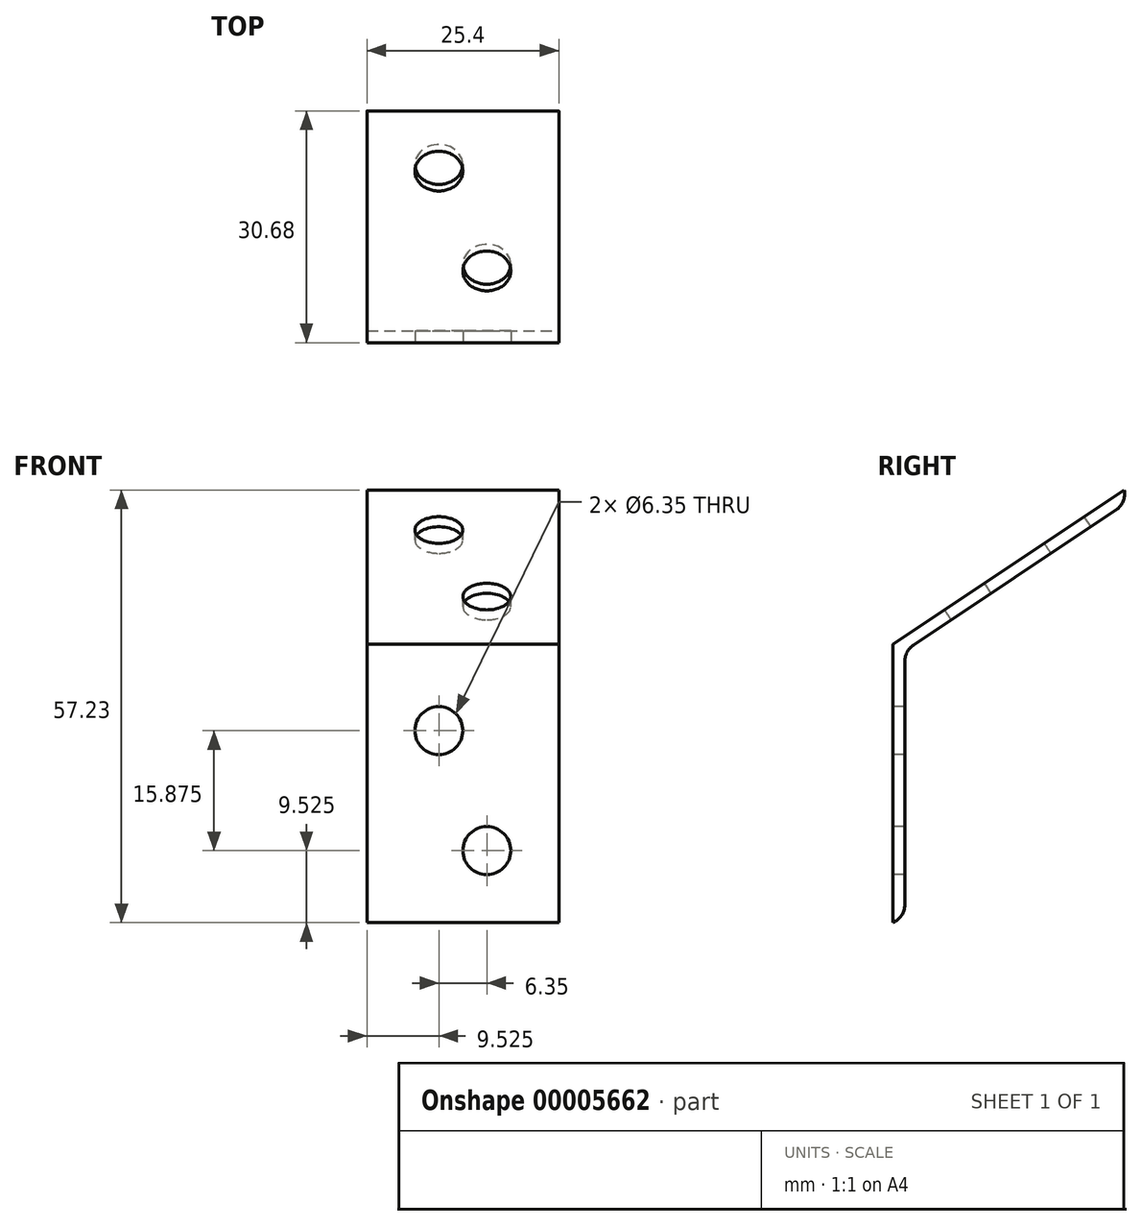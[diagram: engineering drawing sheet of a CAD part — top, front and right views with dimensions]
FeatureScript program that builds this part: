
annotation { "Feature Type Name" : "Feature", "Feature Type Description" : "" }
export const myFeature = defineFeature(function(context is Context, id is Id, definition is map)
    precondition{}
    {
        {
            var Q0;
            Q0=qCreatedBy(makeId("Right.planeOp"),FACE);
            var sketch = newSketch(context, id + "F0", { "sketchPlane" : qUnion([Q0])});
            skLineSegment(sketch, "E0.bottom", {"start": v(0, 0) * mm, "end": v(-1.59, 0) * mm});
            skLineSegment(sketch, "E0.left", {"start": v(0, 0) * mm, "end": v(0, 38.1) * mm});
            skLineSegment(sketch, "E0.right", {"start": v(-1.59, 0) * mm, "end": v(-1.59, 38.95) * mm});
            skLineSegment(sketch, "E1", {"start": v(0, 38.1) * mm, "end": v(31.7, 59.23) * mm});
            skLineSegment(sketch, "E2", {"start": v(31.7, 59.23) * mm, "end": v(30.82, 60.55) * mm});
            skLineSegment(sketch, "E3", {"start": v(30.82, 60.55) * mm, "end": v(-1.59, 38.95) * mm});
            skLineSegment(sketch, "E4", {"start": v(0, 0) * mm, "end": v(2.41, 0) * mm, "construction": true});
            skLineSegment(sketch, "E5", {"start": v(2.41, 0) * mm, "end": v(2.41, 36.8) * mm});
            skLineSegment(sketch, "E6", {"start": v(2.41, 36.8) * mm, "end": v(33.04, 57.23) * mm});
            skLineSegment(sketch, "E7", {"start": v(33.04, 57.23) * mm, "end": v(31.7, 59.23) * mm, "construction": true});
            skLineSegment(sketch, "E8", {"start": v(-1.59, 38.95) * mm, "end": v(4, 35.96) * mm});
            skLineSegment(sketch, "E9", {"start": v(33.04, 57.23) * mm, "end": v(33.92, 55.9) * mm});
            skLineSegment(sketch, "E10", {"start": v(33.92, 55.9) * mm, "end": v(4, 35.96) * mm});
            skLineSegment(sketch, "E11", {"start": v(4, 35.96) * mm, "end": v(4, 0) * mm});
            skLineSegment(sketch, "E12", {"start": v(2.41, 0) * mm, "end": v(4, 0) * mm});
            skSolve(sketch);
        }
        {
            var Q0;
            Q0=qSketchRegion(id+"F0",true);
            extrude(context, id + "F1", {"entities" : qUnion([Q0]), "oppositeDirection" : true, "depth" : 25.4 * mm});
        }
        {
            var Q0;
            Q0=makeQuery(id+"F1.opExtrude","SWEPT_FACE",FACE,{"disambiguationData":[OSD([sQuery(id+"F0.wireOp",EDGE,"E0.right")])]});
            var sketch = newSketch(context, id + "F2", { "sketchPlane" : qUnion([Q0])});
            skCircle(sketch, "E13", {"center": v(-15.88, 25.4) * mm, "radius": 3.18 * mm});
            skCircle(sketch, "E14", {"center": v(-9.53, 9.52) * mm, "radius": 3.18 * mm});
            skSolve(sketch);
        }
        {
            var Q0;
            Q0=qSketchRegion(id+"F2",true);
            extrude(context, id + "F3", {"entities" : qUnion([Q0]), "operationType" : NewBodyOperationType.REMOVE, "oppositeDirection" : true, "depth" : 25.4 * mm});
        }
        {
            var Q0;
            Q0=makeQuery(id+"F1.opExtrude","SWEPT_FACE",FACE,{"disambiguationData":[OSD([sQuery(id+"F0.wireOp",EDGE,"E3")])]});
            var sketch = newSketch(context, id + "F4", { "sketchPlane" : qUnion([Q0])});
            skCircle(sketch, "E15", {"center": v(-9.53, 33.83) * mm, "radius": 3.18 * mm});
            skCircle(sketch, "E16", {"center": v(-15.88, 49.7) * mm, "radius": 3.18 * mm});
            skSolve(sketch);
        }
        {
            var Q0;
            Q0=qSketchRegion(id+"F4",true);
            extrude(context, id + "F5", {"entities" : qUnion([Q0]), "operationType" : NewBodyOperationType.REMOVE, "oppositeDirection" : true, "depth" : 25.4 * mm});
        }
        {
            var Q0;
            Q0=makeQuery(id+"F1.opExtrude","SWEPT_EDGE",EDGE,{"disambiguationData":[OSD([sQuery(id+"F0.wireOp",EDGE,"E0.right"),sQuery(id+"F0.wireOp",EDGE,"E3")])]});
            var Q1;
            Q1=makeQuery(id+"F1.opExtrude","SWEPT_EDGE",EDGE,{"disambiguationData":[OSD([sQuery(id+"F0.wireOp",EDGE,"E2"),sQuery(id+"F0.wireOp",EDGE,"E3")])]});
            var Q2;
            Q2=makeQuery(id+"F1.opExtrude","SWEPT_EDGE",EDGE,{"disambiguationData":[OSD([sQuery(id+"F0.wireOp",EDGE,"E0.bottom"),sQuery(id+"F0.wireOp",EDGE,"E0.right")])]});
            fillet(context, id + "F6", {"entities" : qUnion([Q0, Q1, Q2]), "radius" : 2.54 * mm, "tangentPropagation" : true, "allowEdgeOverflow" : false});
        }
        {
            var Q0;
            Q0=makeQuery(id+"F1.opExtrude","SWEPT_BODY",BODY,{"disambiguationData":[OSD([sQuery(id+"F0.wireOp",EDGE,"E0.bottom"),sQuery(id+"F0.wireOp",EDGE,"E0.left"),sQuery(id+"F0.wireOp",EDGE,"E0.right"),sQuery(id+"F0.wireOp",EDGE,"E1"),sQuery(id+"F0.wireOp",EDGE,"E2"),sQuery(id+"F0.wireOp",EDGE,"E3")])]});
            deleteBodies(context, id + "F7", {"entities" : qUnion([Q0])});
        }
        {
            var Q0;
            Q0=makeQuery(id+"F1.opExtrude","SWEPT_EDGE",EDGE,{"disambiguationData":[OSD([sQuery(id+"F0.wireOp",EDGE,"E9"),sQuery(id+"F0.wireOp",EDGE,"E10")])]});
            var Q1;
            Q1=makeQuery(id+"F1.opExtrude","SWEPT_EDGE",EDGE,{"disambiguationData":[OSD([sQuery(id+"F0.wireOp",EDGE,"E11"),sQuery(id+"F0.wireOp",EDGE,"E12")])]});
            var Q2;
            Q2=makeQuery(id+"F1.opExtrude","SWEPT_EDGE",EDGE,{"disambiguationData":[OSD([sQuery(id+"F0.wireOp",EDGE,"E8"),sQuery(id+"F0.wireOp",EDGE,"E10"),sQuery(id+"F0.wireOp",EDGE,"E11")])]});
            fillet(context, id + "F8", {"entities" : qUnion([Q0, Q1, Q2]), "radius" : 2.54 * mm, "tangentPropagation" : true, "allowEdgeOverflow" : false});
        }
    });
